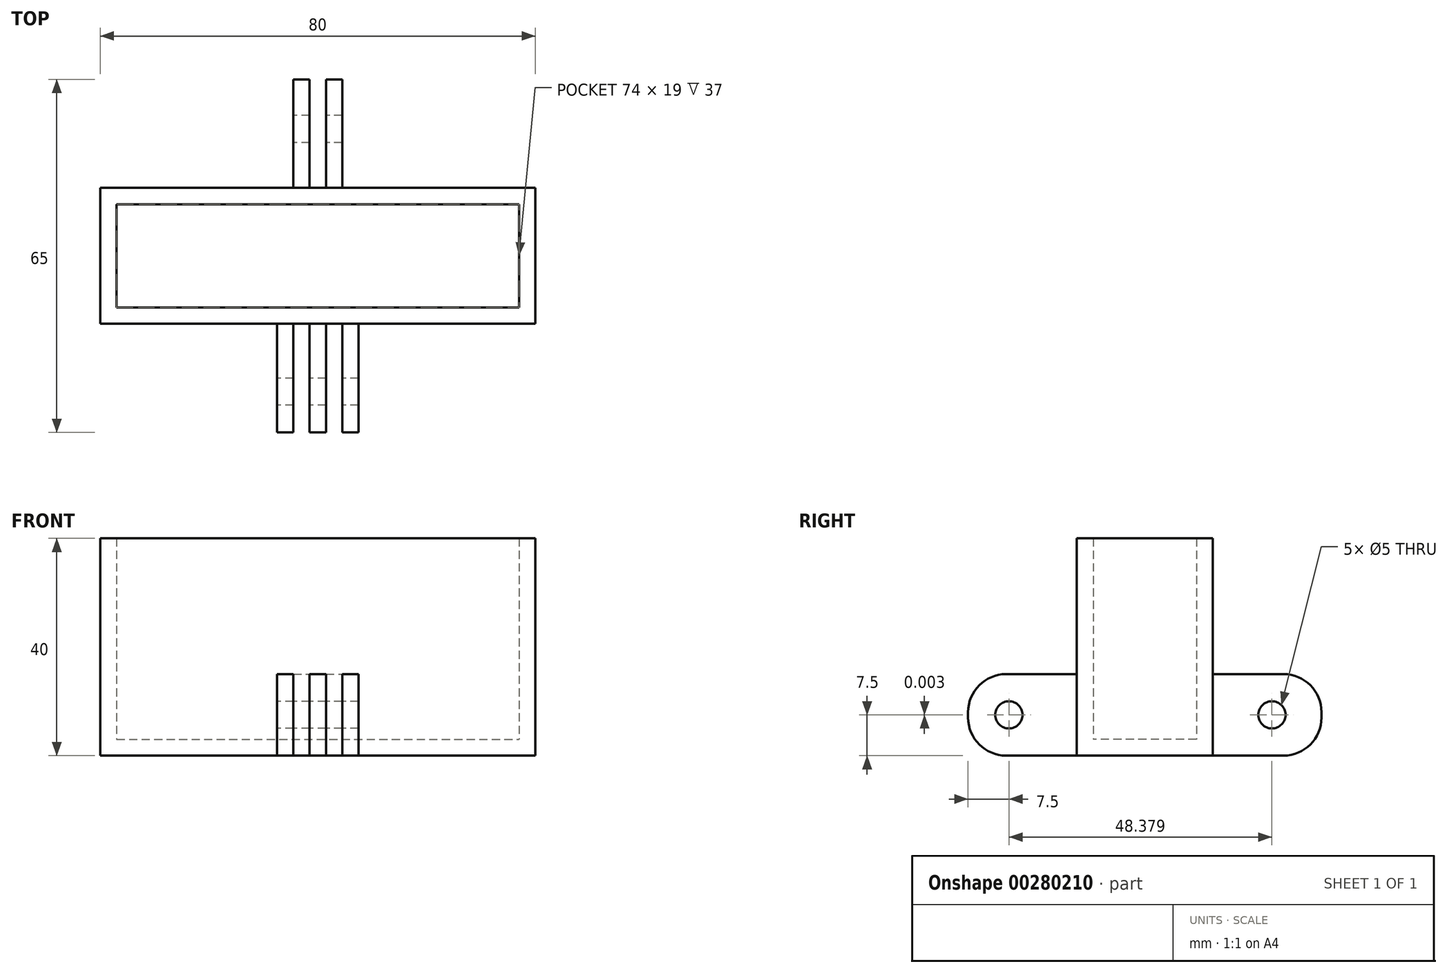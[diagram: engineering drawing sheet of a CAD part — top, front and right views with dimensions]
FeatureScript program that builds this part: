
annotation { "Feature Type Name" : "Feature", "Feature Type Description" : "" }
export const myFeature = defineFeature(function(context is Context, id is Id, definition is map)
    precondition{}
    {
        {
            var Q0;
            Q0=qCreatedBy(makeId("Top.planeOp"),FACE);
            var sketch = newSketch(context, id + "F0", { "sketchPlane" : qUnion([Q0])});
            skLineSegment(sketch, "E0.bottom", {"start": v(-40, 12.5) * mm, "end": v(40, 12.5) * mm});
            skLineSegment(sketch, "E0.top", {"start": v(-40, -12.5) * mm, "end": v(40, -12.5) * mm});
            skLineSegment(sketch, "E0.left", {"start": v(-40, 12.5) * mm, "end": v(-40, -12.5) * mm});
            skLineSegment(sketch, "E0.right", {"start": v(40, 12.5) * mm, "end": v(40, -12.5) * mm});
            skSolve(sketch);
        }
        {
            var Q0;
            Q0=makeQuery(id+"F0.imprint","IMPRINT",FACE,{"disambiguationData":[TD([[makeQuery(id+"F0.imprint","IMPRINT",EDGE,{"derivedFrom":sQuery(id+"F0.wireOp",EDGE,"E0.bottom")}),-1.0]])]});
            extrude(context, id + "F1", {"entities" : qUnion([Q0]), "depth" : 40 * mm});
        }
        {
            var Q0;
            Q0=makeQuery(id+"F1.opExtrude","CAP_FACE",FACE,{"disambiguationData":[OSD([sQuery(id+"F0.wireOp",EDGE,"E0.bottom"),sQuery(id+"F0.wireOp",EDGE,"E0.top"),sQuery(id+"F0.wireOp",EDGE,"E0.left"),sQuery(id+"F0.wireOp",EDGE,"E0.right")])],"isStart":true});
            var sketch = newSketch(context, id + "F2", { "sketchPlane" : qUnion([Q0])});
            skLineSegment(sketch, "E1.bottom", {"start": v(-7.5, 32.5) * mm, "end": v(-4.5, 32.5) * mm});
            skLineSegment(sketch, "E1.top", {"start": v(-7.5, 12.5) * mm, "end": v(-4.5, 12.5) * mm});
            skLineSegment(sketch, "E1.left", {"start": v(-7.5, 32.5) * mm, "end": v(-7.5, 12.5) * mm});
            skLineSegment(sketch, "E1.right", {"start": v(-4.5, 32.5) * mm, "end": v(-4.5, 12.5) * mm});
            skLineSegment(sketch, "E2.bottom", {"start": v(-1.5, 32.5) * mm, "end": v(1.5, 32.5) * mm});
            skLineSegment(sketch, "E2.top", {"start": v(-1.5, 12.5) * mm, "end": v(1.5, 12.5) * mm});
            skLineSegment(sketch, "E2.left", {"start": v(-1.5, 32.5) * mm, "end": v(-1.5, 12.5) * mm});
            skLineSegment(sketch, "E2.right", {"start": v(1.5, 32.5) * mm, "end": v(1.5, 12.5) * mm});
            skLineSegment(sketch, "E3.bottom", {"start": v(4.5, 32.5) * mm, "end": v(7.5, 32.5) * mm});
            skLineSegment(sketch, "E3.top", {"start": v(4.5, 12.5) * mm, "end": v(7.5, 12.5) * mm});
            skLineSegment(sketch, "E3.left", {"start": v(4.5, 32.5) * mm, "end": v(4.5, 12.5) * mm});
            skLineSegment(sketch, "E3.right", {"start": v(7.5, 32.5) * mm, "end": v(7.5, 12.5) * mm});
            skLineSegment(sketch, "E4.bottom", {"start": v(-4.5, -12.5) * mm, "end": v(-1.5, -12.5) * mm});
            skLineSegment(sketch, "E4.top", {"start": v(-4.5, -32.5) * mm, "end": v(-1.5, -32.5) * mm});
            skLineSegment(sketch, "E4.left", {"start": v(-4.5, -12.5) * mm, "end": v(-4.5, -32.5) * mm});
            skLineSegment(sketch, "E4.right", {"start": v(-1.5, -12.5) * mm, "end": v(-1.5, -32.5) * mm});
            skLineSegment(sketch, "E5.bottom", {"start": v(1.5, -12.5) * mm, "end": v(4.5, -12.5) * mm});
            skLineSegment(sketch, "E5.top", {"start": v(1.5, -32.5) * mm, "end": v(4.5, -32.5) * mm});
            skLineSegment(sketch, "E5.left", {"start": v(1.5, -12.5) * mm, "end": v(1.5, -32.5) * mm});
            skLineSegment(sketch, "E5.right", {"start": v(4.5, -12.5) * mm, "end": v(4.5, -32.5) * mm});
            skSolve(sketch);
        }
        {
            var Q0;
            Q0=makeQuery(id+"F2.imprint","IMPRINT",FACE,{"disambiguationData":[TD([[makeQuery(id+"F2.imprint","IMPRINT",EDGE,{"derivedFrom":sQuery(id+"F2.wireOp",EDGE,"E1.bottom")}),-1.0]])]});
            var Q1;
            Q1=makeQuery(id+"F2.imprint","IMPRINT",FACE,{"disambiguationData":[TD([[makeQuery(id+"F2.imprint","IMPRINT",EDGE,{"derivedFrom":sQuery(id+"F2.wireOp",EDGE,"E2.bottom")}),-1.0]])]});
            var Q2;
            Q2=makeQuery(id+"F2.imprint","IMPRINT",FACE,{"disambiguationData":[TD([[makeQuery(id+"F2.imprint","IMPRINT",EDGE,{"derivedFrom":sQuery(id+"F2.wireOp",EDGE,"E3.bottom")}),-1.0]])]});
            var Q3;
            Q3=makeQuery(id+"F2.imprint","IMPRINT",FACE,{"disambiguationData":[TD([[makeQuery(id+"F2.imprint","IMPRINT",EDGE,{"derivedFrom":sQuery(id+"F2.wireOp",EDGE,"E5.bottom")}),-1.0]])]});
            var Q4;
            Q4=makeQuery(id+"F2.imprint","IMPRINT",FACE,{"disambiguationData":[TD([[makeQuery(id+"F2.imprint","IMPRINT",EDGE,{"derivedFrom":sQuery(id+"F2.wireOp",EDGE,"E4.bottom")}),-1.0]])]});
            extrude(context, id + "F3", {"entities" : qUnion([Q0, Q1, Q2, Q3, Q4]), "operationType" : NewBodyOperationType.ADD, "oppositeDirection" : true, "depth" : 15 * mm});
        }
        {
            var Q0;
            Q0=makeQuery(id+"F3.opExtrude","CAP_EDGE",EDGE,{"disambiguationData":[OSD([sQuery(id+"F2.wireOp",EDGE,"E5.top")])],"isStart":true});
            var Q1;
            Q1=makeQuery(id+"F3.opExtrude","CAP_EDGE",EDGE,{"disambiguationData":[OSD([sQuery(id+"F2.wireOp",EDGE,"E4.top")])],"isStart":true});
            var Q2;
            Q2=makeQuery(id+"F3.opExtrude","CAP_EDGE",EDGE,{"disambiguationData":[OSD([sQuery(id+"F2.wireOp",EDGE,"E4.top")])],"isStart":false});
            var Q3;
            Q3=makeQuery(id+"F3.opExtrude","CAP_EDGE",EDGE,{"disambiguationData":[OSD([sQuery(id+"F2.wireOp",EDGE,"E5.top")])],"isStart":false});
            fillet(context, id + "F4", {"entities" : qUnion([Q0, Q1, Q2, Q3]), "radius" : 7 * mm, "tangentPropagation" : true, "allowEdgeOverflow" : false});
        }
        {
            var Q0;
            Q0=makeQuery(id+"F3.opExtrude","CAP_EDGE",EDGE,{"disambiguationData":[OSD([sQuery(id+"F2.wireOp",EDGE,"E1.bottom")])],"isStart":false});
            var Q1;
            Q1=makeQuery(id+"F3.opExtrude","CAP_EDGE",EDGE,{"disambiguationData":[OSD([sQuery(id+"F2.wireOp",EDGE,"E2.bottom")])],"isStart":false});
            var Q2;
            Q2=makeQuery(id+"F3.opExtrude","CAP_EDGE",EDGE,{"disambiguationData":[OSD([sQuery(id+"F2.wireOp",EDGE,"E3.bottom")])],"isStart":false});
            var Q3;
            Q3=makeQuery(id+"F3.opExtrude","CAP_EDGE",EDGE,{"disambiguationData":[OSD([sQuery(id+"F2.wireOp",EDGE,"E3.bottom")])],"isStart":true});
            var Q4;
            Q4=makeQuery(id+"F3.opExtrude","CAP_EDGE",EDGE,{"disambiguationData":[OSD([sQuery(id+"F2.wireOp",EDGE,"E2.bottom")])],"isStart":true});
            var Q5;
            Q5=makeQuery(id+"F3.opExtrude","CAP_EDGE",EDGE,{"disambiguationData":[OSD([sQuery(id+"F2.wireOp",EDGE,"E1.bottom")])],"isStart":true});
            fillet(context, id + "F5", {"entities" : qUnion([Q0, Q1, Q2, Q3, Q4, Q5]), "radius" : 7 * mm, "tangentPropagation" : true, "allowEdgeOverflow" : false});
        }
        {
            var Q0;
            Q0=makeQuery(id+"F3.opExtrude","SWEPT_FACE",FACE,{"disambiguationData":[OSD([sQuery(id+"F2.wireOp",EDGE,"E1.left")])]});
            var sketch = newSketch(context, id + "F6", { "sketchPlane" : qUnion([Q0])});
            skCircle(sketch, "E6", {"center": v(25, 7.5) * mm, "radius": 2.5 * mm});
            skSolve(sketch);
        }
        {
            var Q0;
            Q0=sQuery(id+"F6.wireOp",VERTEX,"E6.center");
            var Q1;
            Q1=makeQuery(id+"F1.opExtrude","SWEPT_BODY",BODY,{"disambiguationData":[OSD([sQuery(id+"F0.wireOp",EDGE,"E0.bottom"),sQuery(id+"F0.wireOp",EDGE,"E0.top"),sQuery(id+"F0.wireOp",EDGE,"E0.left"),sQuery(id+"F0.wireOp",EDGE,"E0.right")])]});
            hole(context, id + "F7", {"style" : HoleStyle.SIMPLE, "endStyle" : HoleEndStyle.THROUGH, "holeDiameter" : 5 * mm, "tappedDepth" : 12 * mm, "tapClearance" : 3, "locations" : qUnion([Q0]), "scope" : qUnion([Q1])});
        }
        {
            var Q0;
            Q0=makeQuery(id+"F3.opExtrude","SWEPT_FACE",FACE,{"disambiguationData":[OSD([sQuery(id+"F2.wireOp",EDGE,"E4.left")])]});
            var sketch = newSketch(context, id + "F8", { "sketchPlane" : qUnion([Q0])});
            skPoint(sketch, "E7", {"position": v(-23.38, 7.5) * mm});
            skSolve(sketch);
        }
        {
            var Q0;
            Q0=sQuery(id+"F8.wireOp",VERTEX,"E7");
            var Q1;
            Q1=makeQuery(id+"F1.opExtrude","SWEPT_BODY",BODY,{"disambiguationData":[OSD([sQuery(id+"F0.wireOp",EDGE,"E0.bottom"),sQuery(id+"F0.wireOp",EDGE,"E0.top"),sQuery(id+"F0.wireOp",EDGE,"E0.left"),sQuery(id+"F0.wireOp",EDGE,"E0.right")])]});
            hole(context, id + "F9", {"style" : HoleStyle.SIMPLE, "endStyle" : HoleEndStyle.THROUGH, "holeDiameter" : 5 * mm, "tappedDepth" : 12 * mm, "tapClearance" : 3, "locations" : qUnion([Q0]), "scope" : qUnion([Q1])});
        }
        {
            var Q0;
            Q0=makeQuery(id+"F1.opExtrude","CAP_FACE",FACE,{"disambiguationData":[OSD([sQuery(id+"F0.wireOp",EDGE,"E0.bottom"),sQuery(id+"F0.wireOp",EDGE,"E0.top"),sQuery(id+"F0.wireOp",EDGE,"E0.left"),sQuery(id+"F0.wireOp",EDGE,"E0.right")])],"isStart":false});
            shell(context, id + "F10", {"entities" : qUnion([Q0]), "thickness" : 3 * mm});
        }
    });
